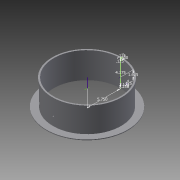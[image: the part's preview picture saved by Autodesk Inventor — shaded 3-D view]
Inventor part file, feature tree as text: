
AUTODESK INVENTOR PART (.ipt)
format: ipt  version: 2015 (Build 190159000, 159)  size: 114,688 bytes
history: native  units: in
note: dims shown in document units (in); Inventor stores cm internally (conversion verified against a paired STEP export)
features: sketch x2, revolve x1, plane x1, hole x1
ambient origin geometry x8: Origin, YZ Plane, XZ Plane, XY Plane, X Axis, Y Axis, Z Axis, Center Point
bodies: Solid1 (feature_tree)
feature tree (5):
  revolve  "Revolution1"  [1 undecoded]
  plane  "Work Plane1"
  hole  "Hole1"  [1 undecoded]
  sketch  "Sketch1"  dims[d0=1.25in d1=0.125in]
  sketch  "Sketch2"  dims[d2=1.125in d3=4.375in d4=0.125in d5=5.75in d6=90.0deg d7=0.125in d8=0.5in d9=1.625in d10=0.275in d11=0.75in d12=0.375in d13=0.25in d14=0.5635in d15=1.0in d16=0.8108in]
note: 2 required parameter values undecoded (feature->parameter linkage not recoverable at this tier; creation-order binding heuristic only, values carry confidence <= 0.55)